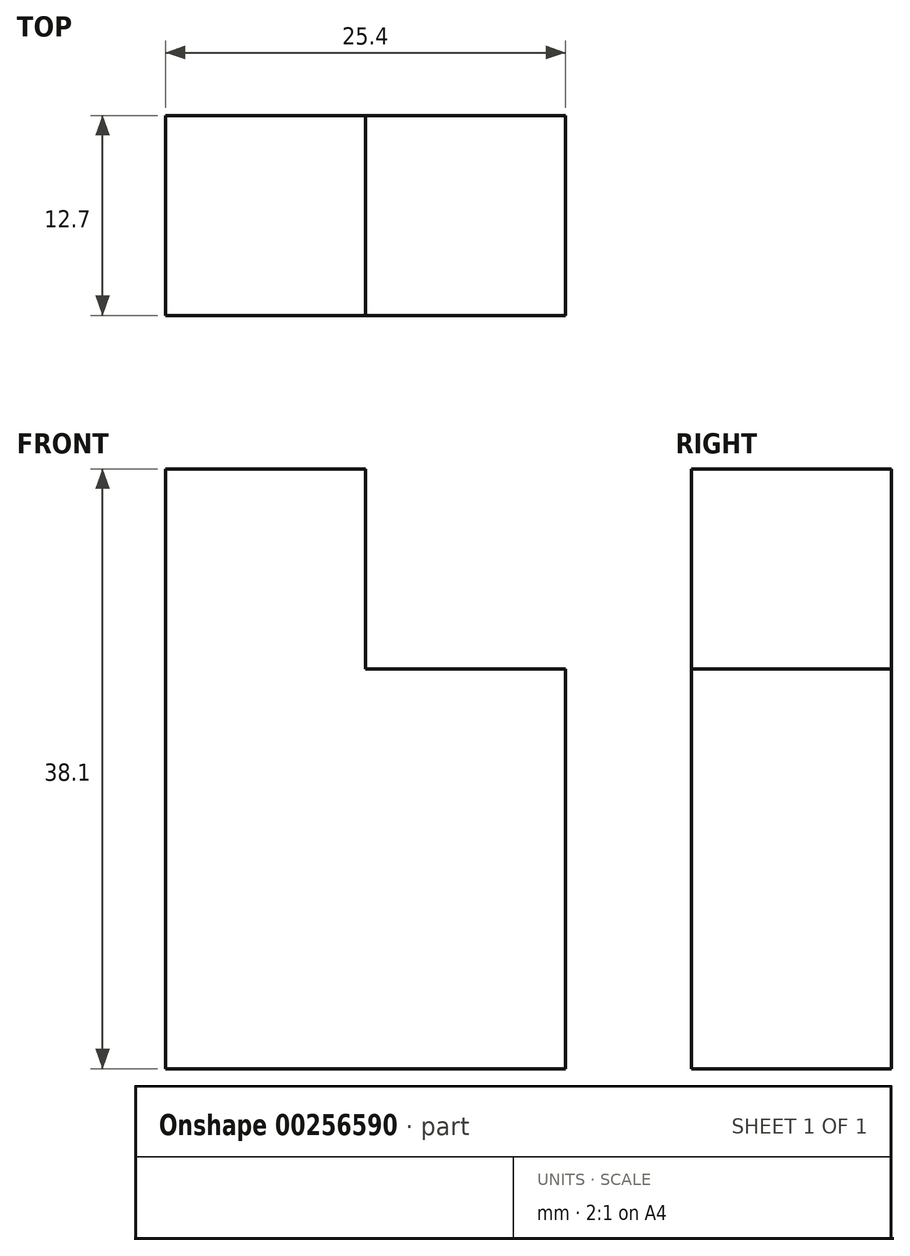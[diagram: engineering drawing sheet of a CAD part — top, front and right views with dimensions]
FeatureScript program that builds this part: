
annotation { "Feature Type Name" : "Feature", "Feature Type Description" : "" }
export const myFeature = defineFeature(function(context is Context, id is Id, definition is map)
    precondition{}
    {
        {
            var Q0;
            Q0=qCreatedBy(makeId("Front.planeOp"),FACE);
            var sketch = newSketch(context, id + "F0", { "sketchPlane" : qUnion([Q0])});
            skLineSegment(sketch, "E0", {"start": v(0, 0) * mm, "end": v(0, 38.1) * mm});
            skLineSegment(sketch, "E1", {"start": v(0, 38.1) * mm, "end": v(12.7, 38.1) * mm});
            skLineSegment(sketch, "E2", {"start": v(12.7, 38.1) * mm, "end": v(12.7, 25.4) * mm});
            skLineSegment(sketch, "E3", {"start": v(12.7, 25.4) * mm, "end": v(25.4, 25.4) * mm});
            skLineSegment(sketch, "E4", {"start": v(25.4, 25.4) * mm, "end": v(25.4, 0) * mm});
            skLineSegment(sketch, "E5", {"start": v(25.4, 0) * mm, "end": v(0, 0) * mm});
            skSolve(sketch);
        }
        {
            var Q0;
            Q0 = qSketchRegion(id + "F0", true);
            extrude(context, id + "F1", {"entities" : qUnion([Q0]), "depth" : 12.7 * mm});
        }
    });
